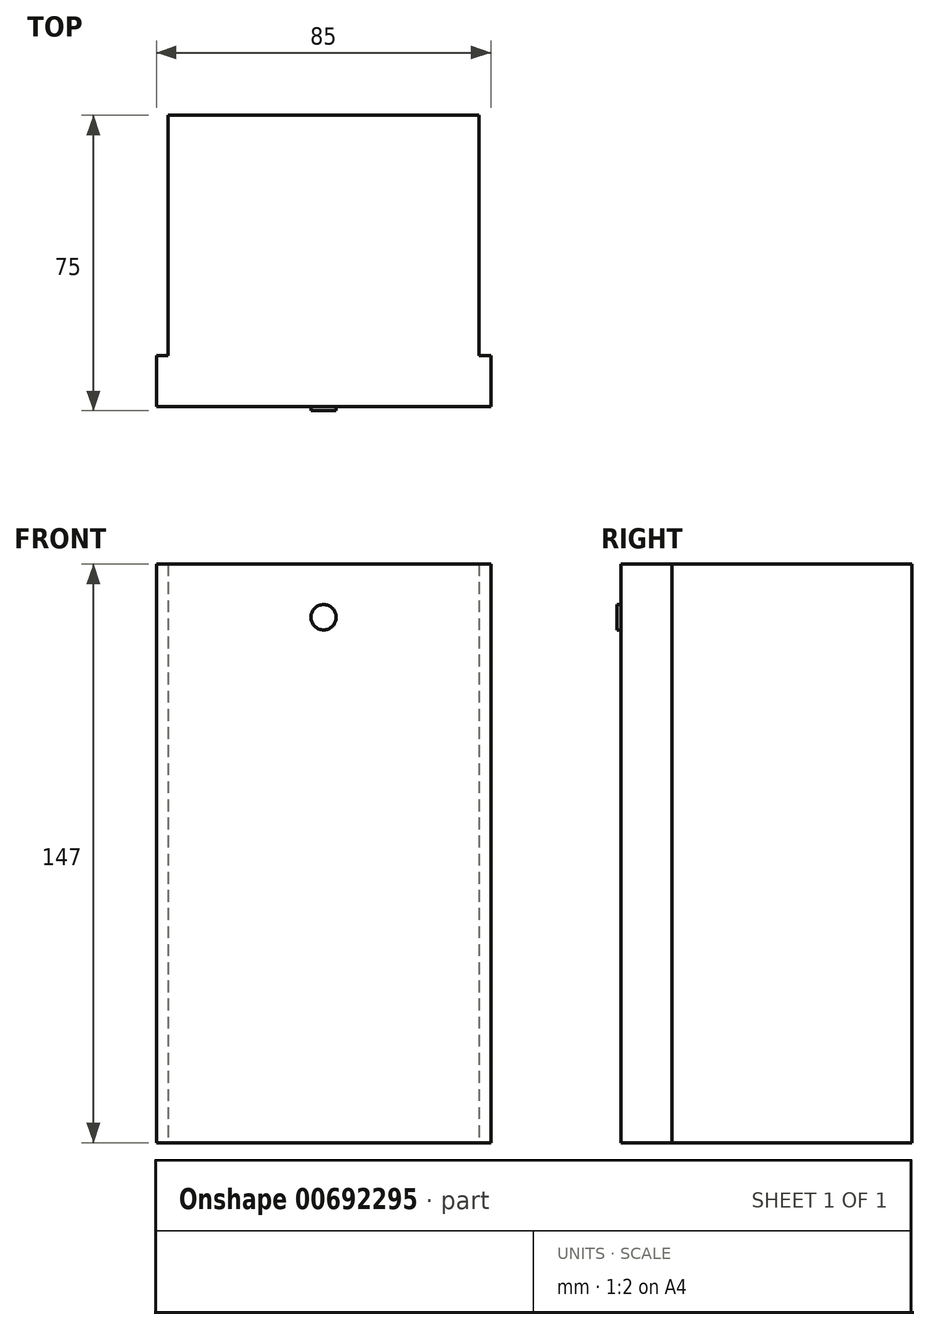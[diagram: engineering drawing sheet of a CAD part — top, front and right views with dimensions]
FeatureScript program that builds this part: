
annotation { "Feature Type Name" : "Feature", "Feature Type Description" : "" }
export const myFeature = defineFeature(function(context is Context, id is Id, definition is map)
    precondition{}
    {
        {
            var Q0;
            Q0=qCreatedBy(makeId("Front.planeOp"),FACE);
            var sketch = newSketch(context, id + "F0", { "sketchPlane" : qUnion([Q0])});
            skLineSegment(sketch, "E0.bottom", {"start": v(42.5, 73.5) * mm, "end": v(-42.5, 73.5) * mm});
            skLineSegment(sketch, "E0.top", {"start": v(42.5, -73.5) * mm, "end": v(-42.5, -73.5) * mm});
            skLineSegment(sketch, "E0.left", {"start": v(42.5, 73.5) * mm, "end": v(42.5, -73.5) * mm});
            skLineSegment(sketch, "E0.right", {"start": v(-42.5, 73.5) * mm, "end": v(-42.5, -73.5) * mm});
            skPoint(sketch, "E0.middle", {"position": v(0, 0) * mm});
            skSolve(sketch);
        }
        {
            var Q0;
            Q0=makeQuery(id+"F0.imprint","IMPRINT",FACE,{"disambiguationData":[TD([[makeQuery(id+"F0.imprint","IMPRINT",EDGE,{"derivedFrom":sQuery(id+"F0.wireOp",EDGE,"E0.bottom")}),1.0]])]});
            extrude(context, id + "F1", {"entities" : qUnion([Q0]), "depth" : 75 * mm, "offsetDistance" : 25 * mm});
        }
        {
            var Q0;
            Q0=makeQuery(id+"F1.opExtrude","CAP_FACE",FACE,{"disambiguationData":[OSD([sQuery(id+"F0.wireOp",EDGE,"E0.bottom"),sQuery(id+"F0.wireOp",EDGE,"E0.top"),sQuery(id+"F0.wireOp",EDGE,"E0.left"),sQuery(id+"F0.wireOp",EDGE,"E0.right")])],"isStart":false});
            var sketch = newSketch(context, id + "F2", { "sketchPlane" : qUnion([Q0])});
            skCircle(sketch, "E1", {"center": v(0, -60) * mm, "radius": 3.21 * mm});
            skCircle(sketch, "E2.MirrorC", {"center": v(0, 60) * mm, "radius": 3.21 * mm});
            skCircle(sketch, "E3", {"center": v(-10, -15) * mm, "radius": 2.5 * mm});
            skLineSegment(sketch, "E4.bottom", {"start": v(26.03, -73.5) * mm, "end": v(27.53, -73.5) * mm});
            skLineSegment(sketch, "E4.top", {"start": v(26.03, 18.5) * mm, "end": v(27.53, 18.5) * mm});
            skLineSegment(sketch, "E4.left", {"start": v(26.03, -73.5) * mm, "end": v(26.03, 18.5) * mm});
            skLineSegment(sketch, "E4.right", {"start": v(27.53, -73.5) * mm, "end": v(27.53, 18.5) * mm});
            skLineSegment(sketch, "E5.1.0.0", {"start": v(29.03, -73.5) * mm, "end": v(29.03, 18.5) * mm});
            skLineSegment(sketch, "E5.1.0.1", {"start": v(30.53, -73.5) * mm, "end": v(30.53, 18.5) * mm});
            skLineSegment(sketch, "E5.1.0.2", {"start": v(29.03, -73.5) * mm, "end": v(30.53, -73.5) * mm});
            skLineSegment(sketch, "E5.1.0.3", {"start": v(29.03, 18.5) * mm, "end": v(30.53, 18.5) * mm});
            skLineSegment(sketch, "E5.2.0.0", {"start": v(32.03, -73.5) * mm, "end": v(32.03, 18.5) * mm});
            skLineSegment(sketch, "E5.2.0.1", {"start": v(33.53, -73.5) * mm, "end": v(33.53, 18.5) * mm});
            skLineSegment(sketch, "E5.2.0.2", {"start": v(32.03, -73.5) * mm, "end": v(33.53, -73.5) * mm});
            skLineSegment(sketch, "E5.2.0.3", {"start": v(32.03, 18.5) * mm, "end": v(33.53, 18.5) * mm});
            skLineSegment(sketch, "E5.direction1", {"start": v(26.03, -73.5) * mm, "end": v(29.03, -73.5) * mm, "construction": true});
            skLineSegment(sketch, "E6.0.1.0", {"start": v(30.53, 61.5) * mm, "end": v(30.53, 73.5) * mm});
            skLineSegment(sketch, "E6.0.1.1", {"start": v(32.03, 61.5) * mm, "end": v(32.03, 73.5) * mm});
            skLineSegment(sketch, "E6.0.1.2", {"start": v(33.53, 61.5) * mm, "end": v(33.53, 73.5) * mm});
            skLineSegment(sketch, "E6.0.1.3", {"start": v(26.03, 61.5) * mm, "end": v(26.03, 73.5) * mm});
            skLineSegment(sketch, "E6.0.1.4", {"start": v(27.53, 61.5) * mm, "end": v(27.53, 73.5) * mm});
            skLineSegment(sketch, "E6.0.1.5", {"start": v(29.03, 61.5) * mm, "end": v(29.03, 73.5) * mm});
            skLineSegment(sketch, "E6.0.1.6", {"start": v(29.03, 153.5) * mm, "end": v(30.53, 153.5) * mm});
            skLineSegment(sketch, "E6.0.1.7", {"start": v(32.03, 61.5) * mm, "end": v(33.53, 61.5) * mm});
            skLineSegment(sketch, "E6.0.1.8", {"start": v(32.03, 153.5) * mm, "end": v(33.53, 153.5) * mm});
            skLineSegment(sketch, "E6.0.1.9", {"start": v(26.03, 153.5) * mm, "end": v(27.53, 153.5) * mm});
            skLineSegment(sketch, "E6.0.1.10", {"start": v(29.03, 61.5) * mm, "end": v(30.53, 61.5) * mm});
            skLineSegment(sketch, "E6.0.1.11", {"start": v(26.03, 61.5) * mm, "end": v(29.03, 61.5) * mm, "construction": true});
            skLineSegment(sketch, "E6.0.1.12", {"start": v(26.03, 61.5) * mm, "end": v(27.53, 61.5) * mm});
            skLineSegment(sketch, "E6.direction1", {"start": v(26.03, -73.5) * mm, "end": v(51.03, -73.5) * mm, "construction": true});
            skLineSegment(sketch, "E6.direction2", {"start": v(26.03, -73.5) * mm, "end": v(26.03, 61.5) * mm, "construction": true});
            skLineSegment(sketch, "E7", {"start": v(42.5, 73.5) * mm, "end": v(19.02, 73.5) * mm});
            skLineSegment(sketch, "E8.left", {"start": v(-33.48, 73.5) * mm, "end": v(-33.48, 40.5) * mm});
            skLineSegment(sketch, "E8.right", {"start": v(-16.48, 73.5) * mm, "end": v(-16.48, 40.5) * mm});
            skArc(sketch, "E9", {"start": v(-33.48, 40.5) * mm, "mid": v(-24.98, 32) * mm, "end": v(-16.48, 40.5) * mm});
            skSolve(sketch);
        }
        {
            var Q0;
            Q0=makeQuery(id+"F2.imprint","IMPRINT",FACE,{"disambiguationData":[TD([[makeQuery(id+"F2.imprint","IMPRINT",EDGE,{"derivedFrom":sQuery(id+"F2.wireOp",EDGE,"E4.bottom")}),-1.0]])]});
            var Q1;
            Q1=makeQuery(id+"F2.imprint","IMPRINT",FACE,{"disambiguationData":[TD([[makeQuery(id+"F2.imprint","IMPRINT",EDGE,{"derivedFrom":sQuery(id+"F2.wireOp",EDGE,"E5.1.0.0")}),-1.0]])]});
            var Q2;
            Q2=makeQuery(id+"F2.imprint","IMPRINT",FACE,{"disambiguationData":[TD([[makeQuery(id+"F2.imprint","IMPRINT",EDGE,{"derivedFrom":sQuery(id+"F2.wireOp",EDGE,"E5.2.0.0")}),-1.0]])]});
            var Q3;
            Q3=makeQuery(id+"F2.imprint","IMPRINT",FACE,{"disambiguationData":[TD([[makeQuery(id+"F2.imprint","IMPRINT",EDGE,{"derivedFrom":sQuery(id+"F2.wireOp",EDGE,"E1")}),1.0]])]});
            var Q4;
            Q4=makeQuery(id+"F2.imprint","IMPRINT",FACE,{"disambiguationData":[TD([[makeQuery(id+"F2.imprint","IMPRINT",EDGE,{"derivedFrom":sQuery(id+"F2.wireOp",EDGE,"E3")}),1.0]])]});
            var Q5;
            Q5=makeQuery(id+"F2.imprint","IMPRINT",FACE,{"disambiguationData":[TD([[makeQuery(id+"F2.imprint","IMPRINT",EDGE,{"derivedFrom":sQuery(id+"F2.wireOp",EDGE,"E2.MirrorC")}),-1.0]])]});
            var Q6;
            {var subQ0=sQuery(id+"F2.wireOp",EDGE,"E8.left");Q6=makeQuery(id+"F2.imprint","IMPRINT",FACE,{"disambiguationData":[TD([[makeQuery(id+"F2.imprint","IMPRINT",EDGE,{"derivedFrom":subQ0}),1.0]])]});}
            var Q7;
            {var subQ0=sQuery(id+"F2.wireOp",EDGE,"E6.0.1.3");Q7=makeQuery(id+"F2.imprint","IMPRINT",FACE,{"disambiguationData":[TD([[makeQuery(id+"F2.imprint","IMPRINT",EDGE,{"derivedFrom":subQ0}),-1.0]])]});}
            var Q8;
            {var subQ0=sQuery(id+"F2.wireOp",EDGE,"E6.0.1.0");Q8=makeQuery(id+"F2.imprint","IMPRINT",FACE,{"disambiguationData":[TD([[makeQuery(id+"F2.imprint","IMPRINT",EDGE,{"derivedFrom":subQ0}),1.0]])]});}
            var Q9;
            {var subQ0=sQuery(id+"F2.wireOp",EDGE,"E6.0.1.1");Q9=makeQuery(id+"F2.imprint","IMPRINT",FACE,{"disambiguationData":[TD([[makeQuery(id+"F2.imprint","IMPRINT",EDGE,{"derivedFrom":subQ0}),-1.0]])]});}
            extrude(context, id + "F3", {"entities" : qUnion([Q0, Q1, Q2, Q3, Q4, Q5, Q6, Q7, Q8, Q9]), "operationType" : NewBodyOperationType.REMOVE, "oppositeDirection" : true, "depth" : 1 * mm, "offsetDistance" : 25 * mm});
        }
        {
            var Q0;
            Q0=makeQuery(id+"F1.opExtrude","SWEPT_FACE",FACE,{"disambiguationData":[OSD([sQuery(id+"F0.wireOp",EDGE,"E0.right")])]});
            var sketch = newSketch(context, id + "F4", { "sketchPlane" : qUnion([Q0])});
            skLineSegment(sketch, "E10.bottom", {"start": v(0, -73.5) * mm, "end": v(61, -73.5) * mm});
            skLineSegment(sketch, "E10.top", {"start": v(0, 73.5) * mm, "end": v(61, 73.5) * mm});
            skLineSegment(sketch, "E10.left", {"start": v(0, -73.5) * mm, "end": v(0, 73.5) * mm});
            skLineSegment(sketch, "E10.right", {"start": v(61, -73.5) * mm, "end": v(61, 73.5) * mm});
            skSolve(sketch);
        }
        {
            var Q0;
            Q0=makeQuery(id+"F4.imprint","IMPRINT",FACE,{"disambiguationData":[TD([[makeQuery(id+"F4.imprint","IMPRINT",EDGE,{"derivedFrom":sQuery(id+"F4.wireOp",EDGE,"E10.bottom")}),-1.0]])]});
            extrude(context, id + "F5", {"entities" : qUnion([Q0]), "operationType" : NewBodyOperationType.REMOVE, "oppositeDirection" : true, "depth" : 3 * mm, "offsetDistance" : 25 * mm});
        }
        {
            var Q0;
            Q0=makeQuery(id+"F1.opExtrude","SWEPT_FACE",FACE,{"disambiguationData":[OSD([sQuery(id+"F0.wireOp",EDGE,"E0.left")])]});
            var sketch = newSketch(context, id + "F6", { "sketchPlane" : qUnion([Q0])});
            skLineSegment(sketch, "E11.bottom", {"start": v(0, -73.5) * mm, "end": v(-61, -73.5) * mm});
            skLineSegment(sketch, "E11.top", {"start": v(0, 73.5) * mm, "end": v(-61, 73.5) * mm});
            skLineSegment(sketch, "E11.left", {"start": v(0, -73.5) * mm, "end": v(0, 73.5) * mm});
            skLineSegment(sketch, "E11.right", {"start": v(-61, -73.5) * mm, "end": v(-61, 73.5) * mm});
            skSolve(sketch);
        }
        {
            var Q0;
            Q0=makeQuery(id+"F6.imprint","IMPRINT",FACE,{"disambiguationData":[TD([[makeQuery(id+"F6.imprint","IMPRINT",EDGE,{"derivedFrom":sQuery(id+"F6.wireOp",EDGE,"E11.bottom")}),1.0]])]});
            extrude(context, id + "F7", {"entities" : qUnion([Q0]), "operationType" : NewBodyOperationType.REMOVE, "oppositeDirection" : true, "depth" : 3 * mm, "offsetDistance" : 25 * mm});
        }
    });
